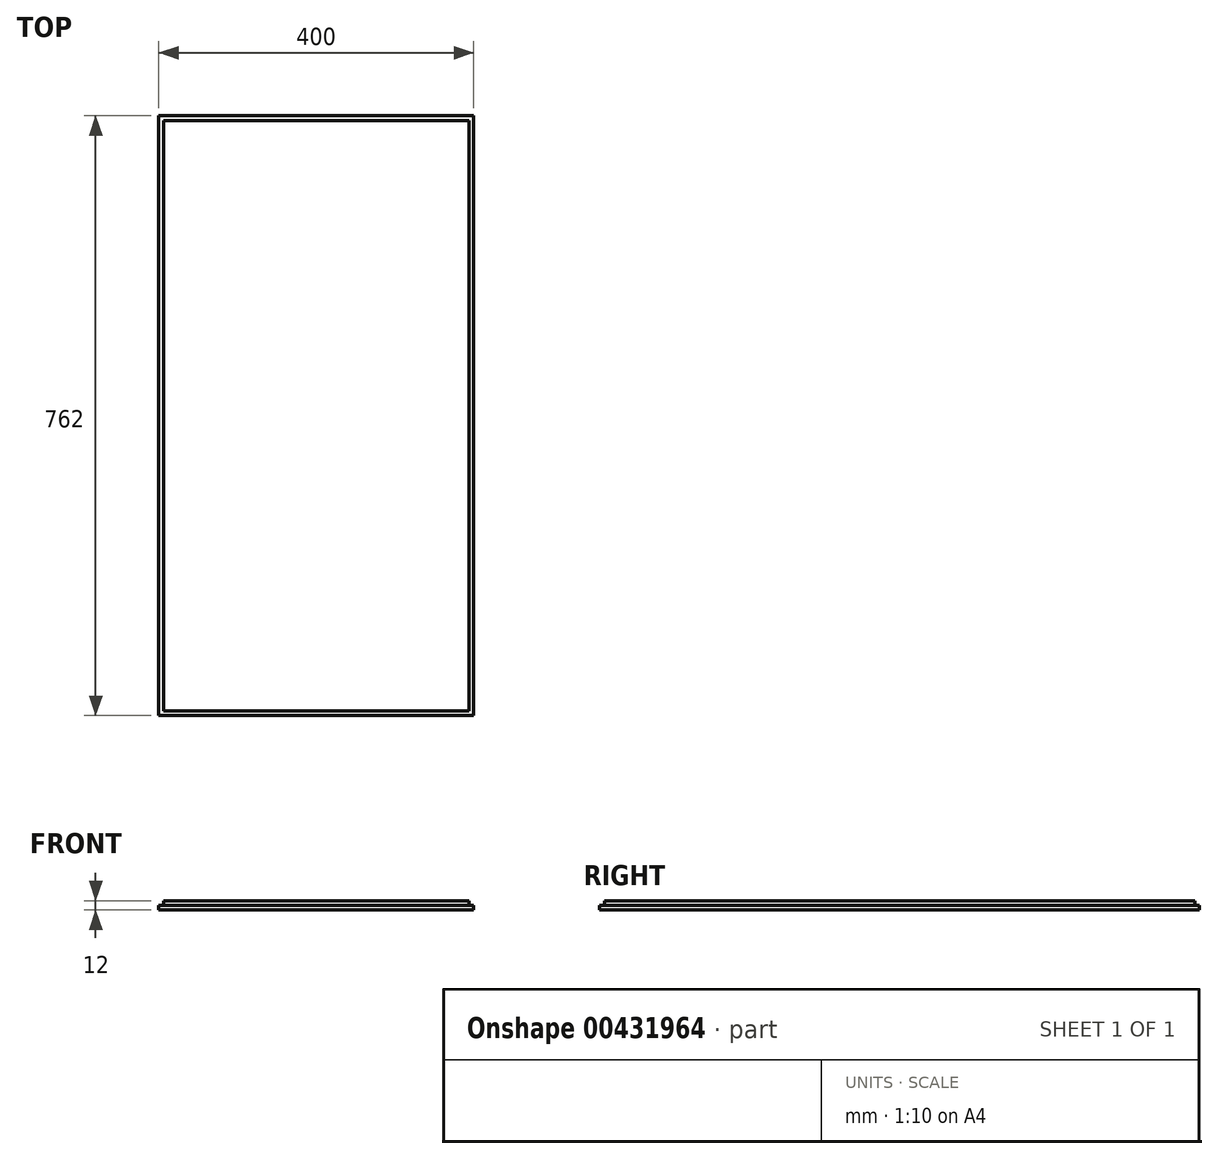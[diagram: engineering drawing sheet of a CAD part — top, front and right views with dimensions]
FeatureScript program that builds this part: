
annotation { "Feature Type Name" : "Feature", "Feature Type Description" : "" }
export const myFeature = defineFeature(function(context is Context, id is Id, definition is map)
    precondition{}
    {
        {
            var Q0;
            Q0=qCreatedBy(makeId("Top.planeOp"),FACE);
            var sketch = newSketch(context, id + "F0", { "sketchPlane" : qUnion([Q0])});
            skLineSegment(sketch, "E0.bottom", {"start": v(-200, 381) * mm, "end": v(200, 381) * mm});
            skLineSegment(sketch, "E0.top", {"start": v(-200, -381) * mm, "end": v(200, -381) * mm});
            skLineSegment(sketch, "E0.left", {"start": v(-200, 381) * mm, "end": v(-200, -381) * mm});
            skLineSegment(sketch, "E0.right", {"start": v(200, 381) * mm, "end": v(200, -381) * mm});
            skPoint(sketch, "E0.middle", {"position": v(0, 0) * mm});
            skSolve(sketch);
        }
        {
            var Q0;
            Q0=makeQuery(id+"F0.imprint","IMPRINT",FACE,{"disambiguationData":[TD([[makeQuery(id+"F0.imprint","IMPRINT",EDGE,{"derivedFrom":sQuery(id+"F0.wireOp",EDGE,"E0.bottom")}),-1.0]])]});
            extrude(context, id + "F1", {"entities" : qUnion([Q0]), "depth" : 12 * mm, "offsetDistance" : 25 * mm});
        }
        {
            var Q0;
            Q0=makeQuery(id+"F1.opExtrude","CAP_FACE",FACE,{"disambiguationData":[OSD([sQuery(id+"F0.wireOp",EDGE,"E0.bottom"),sQuery(id+"F0.wireOp",EDGE,"E0.top"),sQuery(id+"F0.wireOp",EDGE,"E0.left"),sQuery(id+"F0.wireOp",EDGE,"E0.right")])],"isStart":false});
            var sketch = newSketch(context, id + "F2", { "sketchPlane" : qUnion([Q0])});
            skLineSegment(sketch, "E1.bottom", {"start": v(-200, 381) * mm, "end": v(-194, 381) * mm});
            skLineSegment(sketch, "E1.top", {"start": v(-200, -381) * mm, "end": v(-194, -381) * mm});
            skLineSegment(sketch, "E1.left", {"start": v(-200, 381) * mm, "end": v(-200, -381) * mm});
            skLineSegment(sketch, "E1.right", {"start": v(-194, 381) * mm, "end": v(-194, -381) * mm});
            skSolve(sketch);
        }
        {
            var Q0;
            Q0=makeQuery(id+"F2.imprint","IMPRINT",FACE,{"disambiguationData":[TD([[makeQuery(id+"F2.imprint","IMPRINT",EDGE,{"derivedFrom":sQuery(id+"F2.wireOp",EDGE,"E1.bottom")}),-1.0]])]});
            extrude(context, id + "F3", {"entities" : qUnion([Q0]), "operationType" : NewBodyOperationType.REMOVE, "oppositeDirection" : true, "depth" : 6 * mm, "offsetDistance" : 25 * mm});
        }
        {
            var Q0;
            Q0=makeQuery(id+"F1.opExtrude","CAP_FACE",FACE,{"disambiguationData":[OSD([sQuery(id+"F0.wireOp",EDGE,"E0.bottom"),sQuery(id+"F0.wireOp",EDGE,"E0.top"),sQuery(id+"F0.wireOp",EDGE,"E0.left"),sQuery(id+"F0.wireOp",EDGE,"E0.right")])],"isStart":false});
            var sketch = newSketch(context, id + "F4", { "sketchPlane" : qUnion([Q0])});
            skLineSegment(sketch, "E2.bottom", {"start": v(200, -381) * mm, "end": v(194, -381) * mm});
            skLineSegment(sketch, "E2.top", {"start": v(200, 381) * mm, "end": v(194, 381) * mm});
            skLineSegment(sketch, "E2.left", {"start": v(200, -381) * mm, "end": v(200, 381) * mm});
            skLineSegment(sketch, "E2.right", {"start": v(194, -381) * mm, "end": v(194, 381) * mm});
            skSolve(sketch);
        }
        {
            var Q0;
            Q0=qSketchRegion(id+"F4",true);
            extrude(context, id + "F5", {"entities" : qUnion([Q0]), "operationType" : NewBodyOperationType.REMOVE, "oppositeDirection" : true, "depth" : 6 * mm, "offsetDistance" : 25 * mm});
        }
        {
            var Q0;
            Q0=makeQuery(id+"F1.opExtrude","CAP_FACE",FACE,{"disambiguationData":[OSD([sQuery(id+"F0.wireOp",EDGE,"E0.bottom"),sQuery(id+"F0.wireOp",EDGE,"E0.top"),sQuery(id+"F0.wireOp",EDGE,"E0.left"),sQuery(id+"F0.wireOp",EDGE,"E0.right")])],"isStart":false});
            var sketch = newSketch(context, id + "F6", { "sketchPlane" : qUnion([Q0])});
            skLineSegment(sketch, "E3.bottom", {"start": v(-194, 381) * mm, "end": v(194, 381) * mm});
            skLineSegment(sketch, "E3.top", {"start": v(-194, 375) * mm, "end": v(194, 375) * mm});
            skLineSegment(sketch, "E3.left", {"start": v(-194, 381) * mm, "end": v(-194, 375) * mm});
            skLineSegment(sketch, "E3.right", {"start": v(194, 381) * mm, "end": v(194, 375) * mm});
            skSolve(sketch);
        }
        {
            var Q0;
            Q0=qSketchRegion(id+"F6",true);
            extrude(context, id + "F7", {"entities" : qUnion([Q0]), "operationType" : NewBodyOperationType.REMOVE, "oppositeDirection" : true, "depth" : 6 * mm, "offsetDistance" : 25 * mm});
        }
        {
            var Q0;
            {var subQ0=sQuery(id+"F0.wireOp",EDGE,"E0.top");Q0=makeQuery(id+"F7.boolean.opBoolean","SPLIT",FACE,{"disambiguationData":[TD([makeQuery(id+"F1.opExtrude","SWEPT_FACE",FACE,{"disambiguationData":[OSD([subQ0])]})])],"derivedFrom":makeQuery(id+"F1.opExtrude","CAP_FACE",FACE,{"disambiguationData":[OSD([sQuery(id+"F0.wireOp",EDGE,"E0.bottom"),subQ0,sQuery(id+"F0.wireOp",EDGE,"E0.left"),sQuery(id+"F0.wireOp",EDGE,"E0.right")])],"isStart":false})});}
            var sketch = newSketch(context, id + "F8", { "sketchPlane" : qUnion([Q0])});
            skLineSegment(sketch, "E4.bottom", {"start": v(-194, -381) * mm, "end": v(194, -381) * mm});
            skLineSegment(sketch, "E4.top", {"start": v(-194, -375) * mm, "end": v(194, -375) * mm});
            skLineSegment(sketch, "E4.left", {"start": v(-194, -381) * mm, "end": v(-194, -375) * mm});
            skLineSegment(sketch, "E4.right", {"start": v(194, -381) * mm, "end": v(194, -375) * mm});
            skSolve(sketch);
        }
        {
            var Q0;
            Q0=qSketchRegion(id+"F8",true);
            extrude(context, id + "F9", {"entities" : qUnion([Q0]), "operationType" : NewBodyOperationType.REMOVE, "oppositeDirection" : true, "depth" : 6 * mm, "offsetDistance" : 25 * mm});
        }
    });
